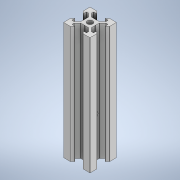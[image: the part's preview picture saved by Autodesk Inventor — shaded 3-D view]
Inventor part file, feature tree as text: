
AUTODESK INVENTOR PART (.ipt)
format: ipt  version: 2021 (Build 250183000, 183)  size: 322,048 bytes
history: native  units: mm
features: sketch x5, hole x3, extrude x2, fillet x2, other x1, pattern_circular x1, projected_geometry x1
ambient origin geometry x8: Origin, YZ Plane, XZ Plane, XY Plane, X Axis, Y Axis, Z Axis, Center Point
bodies: Body1 (feature_tree)
feature tree (15):
  other  "實體1"
  extrude  "擠出1"  Depth=20.0mm
  extrude  "擠出2"  Depth=20.0mm
  fillet  "圓角1"  Radius=88.5mm
  pattern_circular  "環形陣列1"  [2 undecoded]
  hole  "孔1"  [1 undecoded]
  fillet  "圓角2"  Radius=6.2mm
  hole  "孔2"  [1 undecoded]
  hole  "孔3"  [1 undecoded]
  sketch  "草圖1"
  sketch  "草圖2"
  projected_geometry  "投影迴路1"
  sketch  "草圖3"
  sketch  "草圖4"
  sketch  "草圖5"
note: 5 required parameter values undecoded (feature->parameter linkage not recoverable at this tier; creation-order binding heuristic only, values carry confidence <= 0.55)
